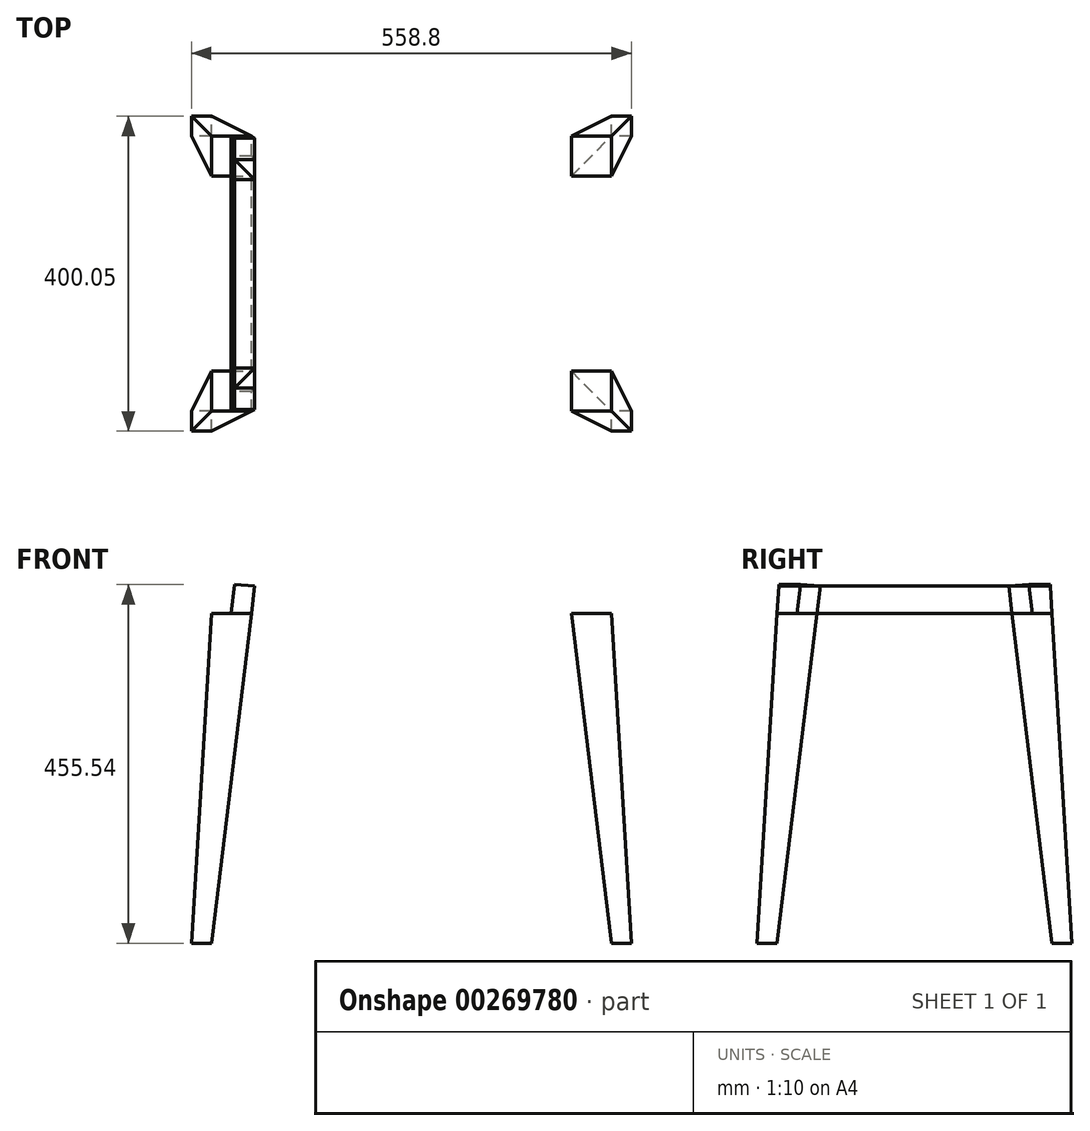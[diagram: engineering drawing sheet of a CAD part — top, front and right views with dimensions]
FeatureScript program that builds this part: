
annotation { "Feature Type Name" : "Feature", "Feature Type Description" : "" }
export const myFeature = defineFeature(function(context is Context, id is Id, definition is map)
    precondition{}
    {
        {
            var Q0;
            Q0=qCreatedBy(makeId("Right.planeOp"),FACE);
            var sketch = newSketch(context, id + "F0", { "sketchPlane" : qUnion([Q0])});
            skLineSegment(sketch, "E0", {"start": v(0, 0) * mm, "end": v(-25.4, 419.1) * mm});
            skLineSegment(sketch, "E1", {"start": v(-25.4, 419.1) * mm, "end": v(-76.2, 419.1) * mm});
            skLineSegment(sketch, "E2", {"start": v(-76.2, 419.1) * mm, "end": v(-25.4, 0) * mm});
            skLineSegment(sketch, "E3", {"start": v(-25.4, 0) * mm, "end": v(0, 0) * mm});
            skLineSegment(sketch, "E4", {"start": v(-323.85, 419.1) * mm, "end": v(-374.65, 0) * mm});
            skLineSegment(sketch, "E5", {"start": v(-374.65, 0) * mm, "end": v(-400.05, 0) * mm});
            skLineSegment(sketch, "E6", {"start": v(-400.05, 0) * mm, "end": v(-374.65, 419.1) * mm});
            skLineSegment(sketch, "E7", {"start": v(-374.65, 419.1) * mm, "end": v(-323.85, 419.1) * mm});
            skLineSegment(sketch, "E8", {"start": v(-374.65, 419.1) * mm, "end": v(-25.4, 419.1) * mm});
            skPoint(sketch, "E9", {"position": v(-200.03, 419.1) * mm});
            skLineSegment(sketch, "E10", {"start": v(-374.65, 419.1) * mm, "end": v(-372.34, 457.2) * mm});
            skLineSegment(sketch, "E11", {"start": v(-372.34, 457.2) * mm, "end": v(-319.62, 454) * mm});
            skLineSegment(sketch, "E12", {"start": v(-319.62, 454) * mm, "end": v(-80.43, 454) * mm});
            skLineSegment(sketch, "E13", {"start": v(-27.7, 457.2) * mm, "end": v(-80.43, 454) * mm});
            skLineSegment(sketch, "E14", {"start": v(-27.7, 457.2) * mm, "end": v(-25.4, 419.1) * mm});
            skPoint(sketch, "E15", {"position": v(-200.03, 454) * mm});
            skLineSegment(sketch, "E16", {"start": v(-76.2, 419.1) * mm, "end": v(-80.43, 454) * mm});
            skLineSegment(sketch, "E17", {"start": v(-80.43, 454) * mm, "end": v(-55.03, 455.54) * mm});
            skLineSegment(sketch, "E18", {"start": v(-55.03, 455.54) * mm, "end": v(-50.61, 419.1) * mm});
            skLineSegment(sketch, "E19", {"start": v(-323.85, 419.1) * mm, "end": v(-319.62, 454) * mm});
            skLineSegment(sketch, "E20", {"start": v(-319.62, 454) * mm, "end": v(-345.02, 455.54) * mm});
            skLineSegment(sketch, "E21", {"start": v(-345.02, 455.54) * mm, "end": v(-349.44, 419.1) * mm});
            skSolve(sketch);
        }
        {
            var Q0;
            Q0=makeQuery(id+"F0.imprint","IMPRINT",FACE,{"disambiguationData":[TD([[makeQuery(id+"F0.imprint","IMPRINT",EDGE,{"derivedFrom":sQuery(id+"F0.wireOp",EDGE,"E13")}),1.0]])]});
            var Q1;
            {var subQ0=sQuery(id+"F0.wireOp",EDGE,"E16");Q1=makeQuery(id+"F0.imprint","IMPRINT",FACE,{"disambiguationData":[TD([[makeQuery(id+"F0.imprint","IMPRINT",EDGE,{"derivedFrom":subQ0}),-1.0]])]});}
            var Q2;
            Q2=makeQuery(id+"F0.imprint","IMPRINT",FACE,{"disambiguationData":[TD([[makeQuery(id+"F0.imprint","IMPRINT",EDGE,{"derivedFrom":sQuery(id+"F0.wireOp",EDGE,"E12")}),-1.0]])]});
            var Q3;
            {var subQ0=sQuery(id+"F0.wireOp",EDGE,"E19");Q3=makeQuery(id+"F0.imprint","IMPRINT",FACE,{"disambiguationData":[TD([[makeQuery(id+"F0.imprint","IMPRINT",EDGE,{"derivedFrom":subQ0}),1.0]])]});}
            var Q4;
            {var subQ0=sQuery(id+"F0.wireOp",EDGE,"E10");Q4=makeQuery(id+"F0.imprint","IMPRINT",FACE,{"disambiguationData":[TD([[makeQuery(id+"F0.imprint","IMPRINT",EDGE,{"derivedFrom":subQ0}),-1.0]])]});}
            extrude(context, id + "F1", {"entities" : qUnion([Q0, Q1, Q2, Q3, Q4]), "depth" : 558.8 * mm, "offsetDistance" : 25.4 * mm});
        }
        {
            var Q0;
            {var subQ0=sQuery(id+"F0.wireOp",EDGE,"E0");Q0=makeQuery(id+"F0.imprint","IMPRINT",FACE,{"disambiguationData":[TD([[makeQuery(id+"F0.imprint","IMPRINT",EDGE,{"derivedFrom":subQ0}),1.0]])]});}
            var Q1;
            {var subQ0=sQuery(id+"F0.wireOp",EDGE,"E4");Q1=makeQuery(id+"F0.imprint","IMPRINT",FACE,{"disambiguationData":[TD([[makeQuery(id+"F0.imprint","IMPRINT",EDGE,{"derivedFrom":subQ0}),-1.0]])]});}
            var Q2;
            {var subQ0=sQuery(id+"F0.wireOp",EDGE,"E16");Q2=makeQuery(id+"F0.imprint","IMPRINT",FACE,{"disambiguationData":[TD([[makeQuery(id+"F0.imprint","IMPRINT",EDGE,{"derivedFrom":subQ0}),-1.0]])]});}
            var Q3;
            {var subQ0=sQuery(id+"F0.wireOp",EDGE,"E19");Q3=makeQuery(id+"F0.imprint","IMPRINT",FACE,{"disambiguationData":[TD([[makeQuery(id+"F0.imprint","IMPRINT",EDGE,{"derivedFrom":subQ0}),1.0]])]});}
            var Q4;
            Q4=makeQuery(id+"F1.opExtrude","CAP_FACE",FACE,{"disambiguationData":[OSD([sQuery(id+"F0.wireOp",EDGE,"E8"),sQuery(id+"F0.wireOp",EDGE,"E10"),sQuery(id+"F0.wireOp",EDGE,"E11"),sQuery(id+"F0.wireOp",EDGE,"E12"),sQuery(id+"F0.wireOp",EDGE,"E13"),sQuery(id+"F0.wireOp",EDGE,"E14")])],"isStart":false});
            extrude(context, id + "F2", {"entities" : qUnion([Q0, Q1, Q2, Q3]), "endBound" : BoundingType.UP_TO_SURFACE, "depth" : 508 * mm, "endBoundEntityFace" : qUnion([Q4]), "offsetDistance" : 25.4 * mm});
        }
        {
            var Q0;
            Q0=qCreatedBy(makeId("Front.planeOp"),FACE);
            var sketch = newSketch(context, id + "F3", { "sketchPlane" : qUnion([Q0])});
            skLineSegment(sketch, "E22", {"start": v(558.8, 0) * mm, "end": v(533.4, 419.1) * mm});
            skLineSegment(sketch, "E23", {"start": v(533.4, 419.1) * mm, "end": v(482.6, 419.1) * mm});
            skLineSegment(sketch, "E24", {"start": v(482.6, 419.1) * mm, "end": v(533.4, 0) * mm});
            skLineSegment(sketch, "E25", {"start": v(533.4, 0) * mm, "end": v(558.8, 0) * mm});
            skLineSegment(sketch, "E26", {"start": v(76.2, 419.1) * mm, "end": v(25.4, 0) * mm});
            skLineSegment(sketch, "E27", {"start": v(25.4, 0) * mm, "end": v(0, 0) * mm});
            skLineSegment(sketch, "E28", {"start": v(0, 0) * mm, "end": v(25.4, 419.1) * mm});
            skLineSegment(sketch, "E29", {"start": v(25.4, 419.1) * mm, "end": v(76.2, 419.1) * mm});
            skLineSegment(sketch, "E30", {"start": v(25.4, 419.1) * mm, "end": v(533.4, 419.1) * mm});
            skPoint(sketch, "E31", {"position": v(279.4, 419.1) * mm});
            skLineSegment(sketch, "E32", {"start": v(25.4, 419.1) * mm, "end": v(27.7, 457.2) * mm});
            skLineSegment(sketch, "E33", {"start": v(27.7, 457.2) * mm, "end": v(80.43, 454) * mm});
            skLineSegment(sketch, "E34", {"start": v(80.43, 454) * mm, "end": v(478.37, 454) * mm});
            skLineSegment(sketch, "E35", {"start": v(531.1, 457.2) * mm, "end": v(478.37, 454) * mm});
            skLineSegment(sketch, "E36", {"start": v(531.1, 457.2) * mm, "end": v(533.4, 419.1) * mm});
            skPoint(sketch, "E37", {"position": v(279.4, 454) * mm});
            skLineSegment(sketch, "E38", {"start": v(27.7, 457.2) * mm, "end": v(531.1, 457.2) * mm});
            skLineSegment(sketch, "E39", {"start": v(27.7, 457.2) * mm, "end": v(0, 457.2) * mm});
            skLineSegment(sketch, "E40", {"start": v(0, 457.2) * mm, "end": v(0, 0) * mm});
            skLineSegment(sketch, "E41", {"start": v(531.1, 457.2) * mm, "end": v(558.8, 457.2) * mm});
            skLineSegment(sketch, "E42", {"start": v(558.8, 457.2) * mm, "end": v(558.8, 0) * mm});
            skLineSegment(sketch, "E43", {"start": v(25.4, 0) * mm, "end": v(533.4, 0) * mm});
            skLineSegment(sketch, "E44", {"start": v(76.2, 419.1) * mm, "end": v(80.43, 454) * mm});
            skLineSegment(sketch, "E45", {"start": v(80.43, 454) * mm, "end": v(55.03, 455.54) * mm});
            skLineSegment(sketch, "E46", {"start": v(55.03, 455.54) * mm, "end": v(50.61, 419.1) * mm});
            skLineSegment(sketch, "E47", {"start": v(482.6, 419.1) * mm, "end": v(478.37, 454) * mm});
            skLineSegment(sketch, "E48", {"start": v(478.37, 454) * mm, "end": v(503.77, 455.54) * mm});
            skLineSegment(sketch, "E49", {"start": v(503.77, 455.54) * mm, "end": v(508.19, 419.1) * mm});
            skSolve(sketch);
        }
        {
            var Q0;
            {var subQ0=sQuery(id+"F3.wireOp",EDGE,"E24");Q0=makeQuery(id+"F3.imprint","IMPRINT",FACE,{"disambiguationData":[TD([[makeQuery(id+"F3.imprint","IMPRINT",EDGE,{"derivedFrom":subQ0}),-1.0]])]});}
            var Q1;
            Q1=makeQuery(id+"F3.imprint","IMPRINT",FACE,{"disambiguationData":[TD([[makeQuery(id+"F3.imprint","IMPRINT",EDGE,{"derivedFrom":sQuery(id+"F3.wireOp",EDGE,"E33")}),1.0]])]});
            var Q2;
            Q2=makeQuery(id+"F3.imprint","IMPRINT",FACE,{"disambiguationData":[TD([[makeQuery(id+"F3.imprint","IMPRINT",EDGE,{"derivedFrom":sQuery(id+"F3.wireOp",EDGE,"E22")}),-1.0]])]});
            var Q3;
            Q3=makeQuery(id+"F3.imprint","IMPRINT",FACE,{"disambiguationData":[TD([[makeQuery(id+"F3.imprint","IMPRINT",EDGE,{"derivedFrom":sQuery(id+"F3.wireOp",EDGE,"E28")}),1.0]])]});
            extrude(context, id + "F4", {"entities" : qUnion([Q0, Q1, Q2, Q3]), "operationType" : NewBodyOperationType.REMOVE, "endBound" : BoundingType.THROUGH_ALL, "depth" : 457.2 * mm, "offsetDistance" : 25.4 * mm});
        }
        {
            var Q0;
            Q0=makeQuery(id+"F3.imprint","IMPRINT",FACE,{"disambiguationData":[TD([[makeQuery(id+"F3.imprint","IMPRINT",EDGE,{"derivedFrom":sQuery(id+"F3.wireOp",EDGE,"E35")}),1.0]])]});
            var Q1;
            {var subQ0=sQuery(id+"F3.wireOp",EDGE,"E32");Q1=makeQuery(id+"F3.imprint","IMPRINT",FACE,{"disambiguationData":[TD([[makeQuery(id+"F3.imprint","IMPRINT",EDGE,{"derivedFrom":subQ0}),-1.0]])]});}
            var Q2;
            Q2=makeQuery(id+"F3.imprint","IMPRINT",FACE,{"disambiguationData":[TD([[makeQuery(id+"F3.imprint","IMPRINT",EDGE,{"derivedFrom":sQuery(id+"F3.wireOp",EDGE,"E34")}),-1.0]])]});
            extrude(context, id + "F5", {"entities" : qUnion([Q0, Q1, Q2]), "operationType" : NewBodyOperationType.REMOVE, "endBound" : BoundingType.THROUGH_ALL, "depth" : 25.4 * mm, "offsetDistance" : 25.4 * mm});
        }
        {
            var Q0;
            Q0=makeQuery(id+"F5.boolean.opBoolean","SPLIT",BODY,{"disambiguationData":[OD(1.0)],"derivedFrom":makeQuery(id+"F2.opExtrude","SWEPT_BODY",BODY,{"disambiguationData":[OSD([sQuery(id+"F0.wireOp",EDGE,"E4"),sQuery(id+"F0.wireOp",EDGE,"E5"),sQuery(id+"F0.wireOp",EDGE,"E6"),sQuery(id+"F0.wireOp",EDGE,"E8"),sQuery(id+"F0.wireOp",EDGE,"E19"),sQuery(id+"F0.wireOp",EDGE,"E20"),sQuery(id+"F0.wireOp",EDGE,"E21")])]})});
            var Q1;
            Q1=makeQuery(id+"F5.boolean.opBoolean","SPLIT",BODY,{"disambiguationData":[OD(0.0)],"derivedFrom":makeQuery(id+"F2.opExtrude","SWEPT_BODY",BODY,{"disambiguationData":[OSD([sQuery(id+"F0.wireOp",EDGE,"E4"),sQuery(id+"F0.wireOp",EDGE,"E5"),sQuery(id+"F0.wireOp",EDGE,"E6"),sQuery(id+"F0.wireOp",EDGE,"E8"),sQuery(id+"F0.wireOp",EDGE,"E19"),sQuery(id+"F0.wireOp",EDGE,"E20"),sQuery(id+"F0.wireOp",EDGE,"E21")])]})});
            var Q2;
            Q2=makeQuery(id+"F5.boolean.opBoolean","SPLIT",BODY,{"disambiguationData":[OD(0.0)],"derivedFrom":makeQuery(id+"F2.opExtrude","SWEPT_BODY",BODY,{"disambiguationData":[OSD([sQuery(id+"F0.wireOp",EDGE,"E0"),sQuery(id+"F0.wireOp",EDGE,"E2"),sQuery(id+"F0.wireOp",EDGE,"E3"),sQuery(id+"F0.wireOp",EDGE,"E8"),sQuery(id+"F0.wireOp",EDGE,"E16"),sQuery(id+"F0.wireOp",EDGE,"E17"),sQuery(id+"F0.wireOp",EDGE,"E18")])]})});
            var Q3;
            Q3=makeQuery(id+"F5.boolean.opBoolean","SPLIT",BODY,{"disambiguationData":[OD(1.0)],"derivedFrom":makeQuery(id+"F2.opExtrude","SWEPT_BODY",BODY,{"disambiguationData":[OSD([sQuery(id+"F0.wireOp",EDGE,"E0"),sQuery(id+"F0.wireOp",EDGE,"E2"),sQuery(id+"F0.wireOp",EDGE,"E3"),sQuery(id+"F0.wireOp",EDGE,"E8"),sQuery(id+"F0.wireOp",EDGE,"E16"),sQuery(id+"F0.wireOp",EDGE,"E17"),sQuery(id+"F0.wireOp",EDGE,"E18")])]})});
            var Q4;
            Q4=makeQuery(id+"F1.opExtrude","SWEPT_BODY",BODY,{"disambiguationData":[OSD([sQuery(id+"F0.wireOp",EDGE,"E8"),sQuery(id+"F0.wireOp",EDGE,"E10"),sQuery(id+"F0.wireOp",EDGE,"E11"),sQuery(id+"F0.wireOp",EDGE,"E12"),sQuery(id+"F0.wireOp",EDGE,"E13"),sQuery(id+"F0.wireOp",EDGE,"E14"),sQuery(id+"F0.wireOp",EDGE,"E17"),sQuery(id+"F0.wireOp",EDGE,"E20")])]});
            booleanBodies(context, id + "F6", {"operationType" : BooleanOperationType.SUBTRACTION, "tools" : qUnion([Q0, Q1, Q2, Q3]), "targets" : qUnion([Q4]), "keepTools" : true});
        }
    });
